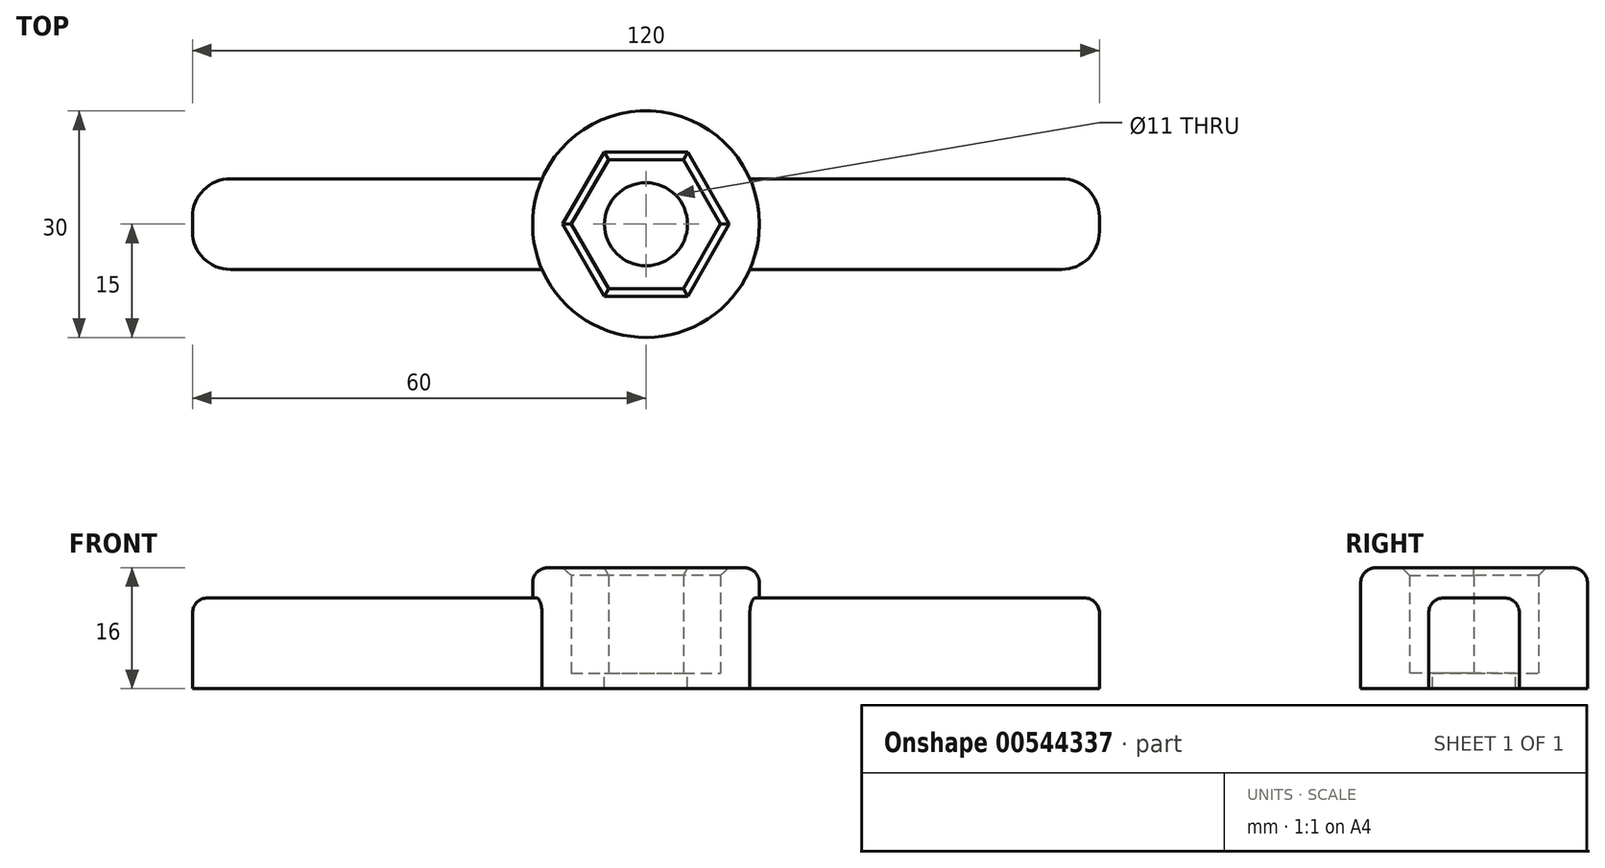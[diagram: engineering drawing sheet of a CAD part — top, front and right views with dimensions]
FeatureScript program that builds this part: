
annotation { "Feature Type Name" : "Feature", "Feature Type Description" : "" }
export const myFeature = defineFeature(function(context is Context, id is Id, definition is map)
    precondition{}
    {
        {
            var Q0;
            Q0=qCreatedBy(makeId("Top.planeOp"),FACE);
            var sketch = newSketch(context, id + "F0", { "sketchPlane" : qUnion([Q0])});
            skCircle(sketch, "E0.cCircle", {"center": v(0, 0) * mm, "radius": 8.55 * mm, "construction": true});
            skLineSegment(sketch, "E0.0", {"start": v(-4.94, 8.55) * mm, "end": v(4.94, 8.55) * mm});
            skLineSegment(sketch, "E0.1", {"start": v(4.94, 8.55) * mm, "end": v(9.87, 0) * mm});
            skLineSegment(sketch, "E0.2", {"start": v(9.87, 0) * mm, "end": v(4.94, -8.55) * mm});
            skLineSegment(sketch, "E0.3", {"start": v(4.94, -8.55) * mm, "end": v(-4.94, -8.55) * mm});
            skLineSegment(sketch, "E0.4", {"start": v(-4.94, -8.55) * mm, "end": v(-9.87, 0) * mm});
            skLineSegment(sketch, "E0.5", {"start": v(-9.87, 0) * mm, "end": v(-4.94, 8.55) * mm});
            skPoint(sketch, "E0.0.midPoint", {"position": v(0, 8.55) * mm});
            skCircle(sketch, "E1", {"center": v(0, 0) * mm, "radius": 15 * mm});
            skSolve(sketch);
        }
        {
            var Q0;
            Q0 = qSketchRegion(id + "F0", true);
            extrude(context, id + "F1", {"entities" : qUnion([Q0]), "depth" : 14 * mm, "offsetDistance" : 25 * mm});
        }
        {
            var Q0;
            Q0=makeQuery(id+"F1.opExtrude","CAP_FACE",FACE,{"disambiguationData":[OSD([sQuery(id+"F0.wireOp",EDGE,"E0.0"),sQuery(id+"F0.wireOp",EDGE,"E0.1"),sQuery(id+"F0.wireOp",EDGE,"E0.2"),sQuery(id+"F0.wireOp",EDGE,"E0.3"),sQuery(id+"F0.wireOp",EDGE,"E0.4"),sQuery(id+"F0.wireOp",EDGE,"E0.5"),sQuery(id+"F0.wireOp",EDGE,"E1")])],"isStart":true});
            var sketch = newSketch(context, id + "F2", { "sketchPlane" : qUnion([Q0])});
            skCircle(sketch, "E2", {"center": v(0, 0) * mm, "radius": 15 * mm});
            skCircle(sketch, "E3", {"center": v(0, 0) * mm, "radius": 5.5 * mm});
            skSolve(sketch);
        }
        {
            var Q0;
            Q0 = qSketchRegion(id + "F2", true);
            extrude(context, id + "F3", {"entities" : qUnion([Q0]), "operationType" : NewBodyOperationType.ADD, "depth" : 2 * mm, "offsetDistance" : 25 * mm});
        }
        {
            var Q0;
            Q0=makeQuery(id+"F3.opExtrude","CAP_FACE",FACE,{"disambiguationData":[OSD([sQuery(id+"F2.wireOp",EDGE,"E2"),sQuery(id+"F2.wireOp",EDGE,"E3")])],"isStart":false});
            var sketch = newSketch(context, id + "F4", { "sketchPlane" : qUnion([Q0])});
            skLineSegment(sketch, "E4.bottom", {"start": v(-13.75, -6) * mm, "end": v(-60, -6) * mm});
            skLineSegment(sketch, "E4.top", {"start": v(-13.75, 6) * mm, "end": v(-60, 6) * mm});
            skLineSegment(sketch, "E4.right", {"start": v(-60, -6) * mm, "end": v(-60, 6) * mm});
            skArc(sketch, "E5.0", {"start": v(-13.75, 6) * mm, "mid": v(-15, 0) * mm, "end": v(-13.75, -6) * mm});
            skSolve(sketch);
        }
        {
            var Q0;
            Q0 = qSketchRegion(id + "F4", true);
            extrude(context, id + "F5", {"entities" : qUnion([Q0]), "operationType" : NewBodyOperationType.ADD, "oppositeDirection" : true, "depth" : 12 * mm, "offsetDistance" : 25 * mm});
        }
        {
            var Q0;
            Q0=makeQuery(id+"F1.opExtrude","SWEPT_BODY",BODY,{"disambiguationData":[OSD([sQuery(id+"F0.wireOp",EDGE,"E0.0"),sQuery(id+"F0.wireOp",EDGE,"E0.1"),sQuery(id+"F0.wireOp",EDGE,"E0.2"),sQuery(id+"F0.wireOp",EDGE,"E0.3"),sQuery(id+"F0.wireOp",EDGE,"E0.4"),sQuery(id+"F0.wireOp",EDGE,"E0.5"),sQuery(id+"F0.wireOp",EDGE,"E1")])]});
            var Q1;
            Q1=qCreatedBy(makeId("Right.planeOp"),FACE);
            mirror(context, id + "F6", {"operationType" : NewBodyOperationType.ADD, "entities" : qUnion([Q0]), "mirrorPlane" : qUnion([Q1])});
        }
        {
            var Q0;
            Q0=makeQuery(id+"F6.opPattern","COPY",EDGE,{"derivedFrom":makeQuery(id+"F5.opExtrude","SWEPT_EDGE",EDGE,{"disambiguationData":[OSD([sQuery(id+"F4.wireOp",EDGE,"E4.bottom"),sQuery(id+"F4.wireOp",EDGE,"E4.right")])]}),"instanceName":"1"});
            var Q1;
            Q1=makeQuery(id+"F6.opPattern","COPY",EDGE,{"derivedFrom":makeQuery(id+"F5.opExtrude","SWEPT_EDGE",EDGE,{"disambiguationData":[OSD([sQuery(id+"F4.wireOp",EDGE,"E4.top"),sQuery(id+"F4.wireOp",EDGE,"E4.right")])]}),"instanceName":"1"});
            var Q2;
            Q2=makeQuery(id+"F5.opExtrude","SWEPT_EDGE",EDGE,{"disambiguationData":[OSD([sQuery(id+"F4.wireOp",EDGE,"E4.bottom"),sQuery(id+"F4.wireOp",EDGE,"E4.right")])]});
            var Q3;
            Q3=makeQuery(id+"F5.opExtrude","SWEPT_EDGE",EDGE,{"disambiguationData":[OSD([sQuery(id+"F4.wireOp",EDGE,"E4.top"),sQuery(id+"F4.wireOp",EDGE,"E4.right")])]});
            fillet(context, id + "F7", {"entities" : qUnion([Q0, Q1, Q2, Q3]), "radius" : 5 * mm, "tangentPropagation" : true, "allowEdgeOverflow" : false});
        }
        {
            var Q0;
            Q0=makeQuery(id+"F6.opPattern","COPY",EDGE,{"derivedFrom":makeQuery(id+"F5.opExtrude","CAP_EDGE",EDGE,{"disambiguationData":[OSD([sQuery(id+"F4.wireOp",EDGE,"E4.bottom")])],"isStart":false}),"instanceName":"1"});
            var Q1;
            Q1=makeQuery(id+"F6.opPattern","COPY",EDGE,{"derivedFrom":makeQuery(id+"F5.opExtrude","SWEPT_EDGE",EDGE,{"disambiguationData":[OSD([sQuery(id+"F2.wireOp",EDGE,"E2"),sQuery(id+"F4.wireOp",EDGE,"E4.bottom"),sQuery(id+"F4.wireOp",EDGE,"E5.0")])]}),"instanceName":"1"});
            var Q2;
            Q2=makeQuery(id+"F5.opExtrude","CAP_EDGE",EDGE,{"disambiguationData":[OSD([sQuery(id+"F4.wireOp",EDGE,"E4.bottom")])],"isStart":false});
            var Q3;
            Q3=makeQuery(id+"F5.opExtrude","SWEPT_EDGE",EDGE,{"disambiguationData":[OSD([sQuery(id+"F2.wireOp",EDGE,"E2"),sQuery(id+"F4.wireOp",EDGE,"E4.bottom"),sQuery(id+"F4.wireOp",EDGE,"E5.0")])]});
            var Q4;
            Q4=makeQuery(id+"F1.opExtrude","CAP_EDGE",EDGE,{"disambiguationData":[OSD([sQuery(id+"F0.wireOp",EDGE,"E1")])],"isStart":false});
            fillet(context, id + "F8", {"entities" : qUnion([Q0, Q1, Q2, Q3, Q4]), "radius" : 2 * mm, "tangentPropagation" : true, "allowEdgeOverflow" : false});
        }
        {
            var Q0;
            Q0=makeQuery(id+"F1.opExtrude","CAP_EDGE",EDGE,{"disambiguationData":[OSD([sQuery(id+"F0.wireOp",EDGE,"E0.0")])],"isStart":false});
            var Q1;
            Q1=makeQuery(id+"F1.opExtrude","CAP_EDGE",EDGE,{"disambiguationData":[OSD([sQuery(id+"F0.wireOp",EDGE,"E0.5")])],"isStart":false});
            var Q2;
            Q2=makeQuery(id+"F1.opExtrude","CAP_EDGE",EDGE,{"disambiguationData":[OSD([sQuery(id+"F0.wireOp",EDGE,"E0.4")])],"isStart":false});
            var Q3;
            Q3=makeQuery(id+"F1.opExtrude","CAP_EDGE",EDGE,{"disambiguationData":[OSD([sQuery(id+"F0.wireOp",EDGE,"E0.3")])],"isStart":false});
            var Q4;
            Q4=makeQuery(id+"F1.opExtrude","CAP_EDGE",EDGE,{"disambiguationData":[OSD([sQuery(id+"F0.wireOp",EDGE,"E0.2")])],"isStart":false});
            var Q5;
            Q5=makeQuery(id+"F1.opExtrude","CAP_EDGE",EDGE,{"disambiguationData":[OSD([sQuery(id+"F0.wireOp",EDGE,"E0.1")])],"isStart":false});
            chamfer(context, id + "F9", {"entities" : qUnion([Q0, Q1, Q2, Q3, Q4, Q5]), "width" : 1 * mm, "tangentPropagation" : true});
        }
    });
